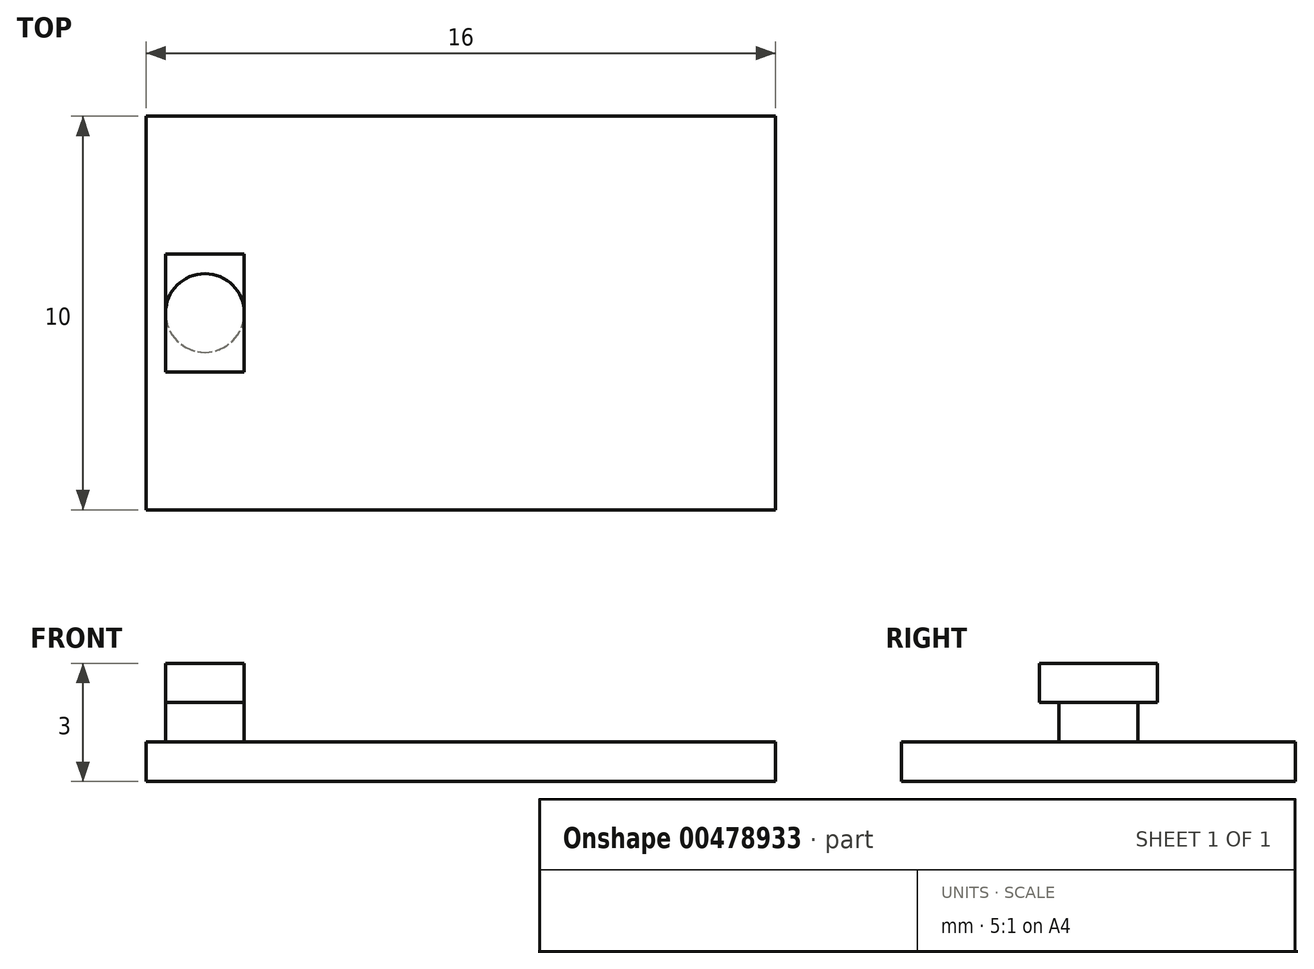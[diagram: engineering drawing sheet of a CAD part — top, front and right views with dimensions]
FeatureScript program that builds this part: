
annotation { "Feature Type Name" : "Feature", "Feature Type Description" : "" }
export const myFeature = defineFeature(function(context is Context, id is Id, definition is map)
    precondition{}
    {
        {
            var Q0;
            Q0=qCreatedBy(makeId("Top.planeOp"),FACE);
            var sketch = newSketch(context, id + "F0", { "sketchPlane" : qUnion([Q0])});
            skLineSegment(sketch, "E0.bottom", {"start": v(8, -5) * mm, "end": v(-8, -5) * mm});
            skLineSegment(sketch, "E0.top", {"start": v(8, 5) * mm, "end": v(-8, 5) * mm});
            skLineSegment(sketch, "E0.left", {"start": v(8, -5) * mm, "end": v(8, 5) * mm});
            skLineSegment(sketch, "E0.right", {"start": v(-8, -5) * mm, "end": v(-8, 5) * mm});
            skPoint(sketch, "E0.middle", {"position": v(0, 0) * mm});
            skCircle(sketch, "E1", {"center": v(-6.5, 0) * mm, "radius": 1 * mm});
            skSolve(sketch);
        }
        {
            var Q0;
            Q0=makeQuery(id+"F0.imprint","IMPRINT",FACE,{"disambiguationData":[TD([[makeQuery(id+"F0.imprint","IMPRINT",EDGE,{"derivedFrom":sQuery(id+"F0.wireOp",EDGE,"E1")}),1.0]])]});
            var Q1;
            Q1=makeQuery(id+"F0.imprint","IMPRINT",FACE,{"disambiguationData":[TD([[makeQuery(id+"F0.imprint","IMPRINT",EDGE,{"derivedFrom":sQuery(id+"F0.wireOp",EDGE,"E0.bottom")}),-1.0]])]});
            extrude(context, id + "F1", {"entities" : qUnion([Q0, Q1]), "oppositeDirection" : true, "depth" : 1 * mm, "offsetDistance" : 25 * mm});
        }
        {
            var Q0;
            Q0=makeQuery(id+"F0.imprint","IMPRINT",FACE,{"disambiguationData":[TD([[makeQuery(id+"F0.imprint","IMPRINT",EDGE,{"derivedFrom":sQuery(id+"F0.wireOp",EDGE,"E1")}),1.0]])]});
            extrude(context, id + "F2", {"entities" : qUnion([Q0]), "operationType" : NewBodyOperationType.ADD, "depth" : 1 * mm, "offsetDistance" : 25 * mm});
        }
        {
            var Q0;
            Q0=makeQuery(id+"F2.opExtrude","CAP_FACE",FACE,{"disambiguationData":[OSD([sQuery(id+"F0.wireOp",EDGE,"E1")])],"isStart":false});
            var sketch = newSketch(context, id + "F3", { "sketchPlane" : qUnion([Q0])});
            skLineSegment(sketch, "E2.bottom", {"start": v(-5, -1) * mm, "end": v(-8, -1) * mm});
            skLineSegment(sketch, "E2.top", {"start": v(-5, 1) * mm, "end": v(-8, 1) * mm});
            skLineSegment(sketch, "E2.left", {"start": v(-5, -1) * mm, "end": v(-5, 1) * mm});
            skLineSegment(sketch, "E2.right", {"start": v(-8, -1) * mm, "end": v(-8, 1) * mm});
            skPoint(sketch, "E2.middle", {"position": v(-6.5, 0) * mm});
            skSolve(sketch);
        }
        {
            var Q0;
            {var subQ0=sQuery(id+"F3.wireOp",EDGE,"E2.left");Q0=makeQuery(id+"F3.imprint","IMPRINT",FACE,{"disambiguationData":[TD([[makeQuery(id+"F3.imprint","IMPRINT",EDGE,{"derivedFrom":subQ0}),1.0]])]});}
            var Q1;
            {var subQ0=sQuery(id+"F3.wireOp",EDGE,"E2.right");Q1=makeQuery(id+"F3.imprint","IMPRINT",FACE,{"disambiguationData":[TD([[makeQuery(id+"F3.imprint","IMPRINT",EDGE,{"derivedFrom":subQ0}),-1.0]])]});}
            var Q2;
            {var subQ0=makeQuery(id+"F2.opExtrude","CAP_EDGE",EDGE,{"disambiguationData":[OSD([sQuery(id+"F0.wireOp",EDGE,"E1")])],"isStart":false});var subQ1=makeQuery(id+"F3.imprint","INTERSECT",VERTEX,{"derivedFrom":[subQ0,sQuery(id+"F3.wireOp",EDGE,"E2.bottom")]});Q2=makeQuery(id+"F3.imprint","IMPRINT",FACE,{"disambiguationData":[TD([[makeQuery(id+"F3.imprint","IMPRINT",EDGE,{"disambiguationData":[TD([[subQ1,-1.0]])],"derivedFrom":subQ0}),1.0]])]});}
            extrude(context, id + "F4", {"entities" : qUnion([Q0, Q1, Q2]), "depth" : 1 * mm, "offsetDistance" : 25 * mm});
        }
        {
            var Q0;
            Q0=makeQuery(id+"F4.opExtrude","SWEPT_FACE",FACE,{"disambiguationData":[OSD([sQuery(id+"F3.wireOp",EDGE,"E2.left")])]});
            var sketch = newSketch(context, id + "F5", { "sketchPlane" : qUnion([Q0])});
            skCircle(sketch, "E3", {"center": v(0, 1.5) * mm, "radius": 0.5 * mm});
            skPoint(sketch, "E3.centerSnap0", {"position": v(0, 1) * mm});
            skSolve(sketch);
        }
        {
            var Q0;
            Q0=qCreatedBy(makeId("Front.planeOp"),FACE);
            var sketch = newSketch(context, id + "F6", { "sketchPlane" : qUnion([Q0])});
            skFitSpline(sketch, "E4", {"points": [v(-5, 1.5) * mm, v(8.74, 6.39) * mm, v(30.58, 8.77) * mm, v(59.3, 16.57) * mm, v(128.9, 62.5) * mm], "startDerivative": vector(77.42, 34.17) * mm, "endDerivative": vector(193.35, 141.12) * mm});
            skSolve(sketch);
        }
        {
            var Q0;
            Q0=makeQuery(id+"F4.opExtrude","SWEPT_BODY",BODY,{"disambiguationData":[OSD([sQuery(id+"F3.wireOp",EDGE,"E2.bottom"),sQuery(id+"F3.wireOp",EDGE,"E2.top"),sQuery(id+"F3.wireOp",EDGE,"E2.left"),sQuery(id+"F3.wireOp",EDGE,"E2.right")])]});
            var Q1;
            Q1=makeQuery(id+"FeewY8r2Xcn23Mt_1.opSweep","SWEPT_BODY",BODY,{"disambiguationData":[OSD([sQuery(id+"F5.wireOp",EDGE,"E3"),sQuery(id+"F6.wireOp",EDGE,"E4")])]});
            var Q2;
            Q2=sQuery(id+"F0.wireOp",EDGE,"E1");
            transform(context, id + "F7", {"entities" : qUnion([Q0, Q1]), "transformType" : TransformType.ROTATION, "transformAxis" : qUnion([Q2]), "angle" : 90 * degree, "makeCopy" : false});
        }
    });
